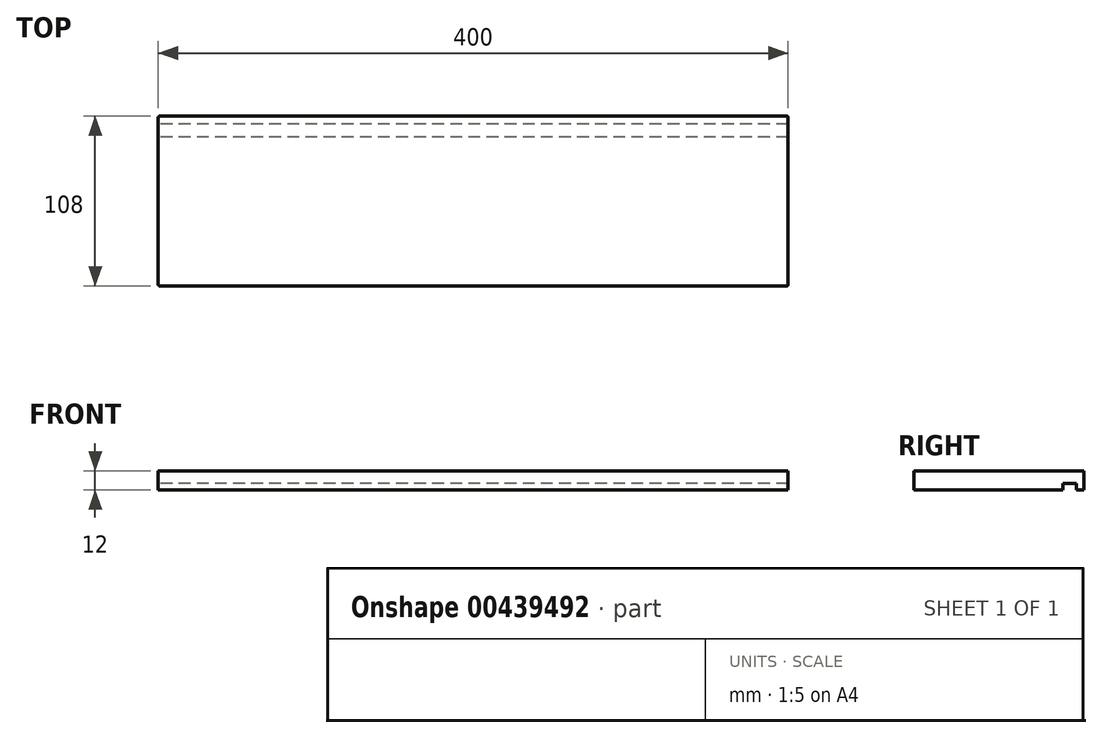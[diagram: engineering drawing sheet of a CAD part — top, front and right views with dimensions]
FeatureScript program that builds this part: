
annotation { "Feature Type Name" : "Feature", "Feature Type Description" : "" }
export const myFeature = defineFeature(function(context is Context, id is Id, definition is map)
    precondition{}
    {
        {
            var Q0;
            Q0=qCreatedBy(makeId("Right.planeOp"),FACE);
            var sketch = newSketch(context, id + "F0", { "sketchPlane" : qUnion([Q0])});
            skLineSegment(sketch, "E0.top", {"start": v(0, 12) * mm, "end": v(108, 12) * mm});
            skLineSegment(sketch, "E0.left", {"start": v(0, 0) * mm, "end": v(0, 12) * mm});
            skLineSegment(sketch, "E0.right", {"start": v(108, 0) * mm, "end": v(108, 12) * mm});
            skLineSegment(sketch, "E1", {"start": v(108, 0) * mm, "end": v(103, 0) * mm});
            skLineSegment(sketch, "E2", {"start": v(103, 0) * mm, "end": v(103, 4) * mm});
            skLineSegment(sketch, "E3", {"start": v(103, 4) * mm, "end": v(94.5, 4) * mm});
            skLineSegment(sketch, "E4", {"start": v(94.5, 4) * mm, "end": v(94.5, 0) * mm});
            skLineSegment(sketch, "E5", {"start": v(94.5, 0) * mm, "end": v(0, 0) * mm});
            skSolve(sketch);
        }
        {
            var Q0;
            Q0=makeQuery(id+"F0.imprint","IMPRINT",FACE,{"disambiguationData":[TD([[makeQuery(id+"F0.imprint","IMPRINT",EDGE,{"derivedFrom":sQuery(id+"F0.wireOp",EDGE,"E0.top")}),-1.0]])]});
            extrude(context, id + "F1", {"entities" : qUnion([Q0]), "depth" : 400 * mm, "offsetDistance" : 25 * mm, "symmetric" : true});
        }
        {
            var Q0;
            Q0=makeQuery(id+"F1.opExtrude","CAP_EDGE",EDGE,{"disambiguationData":[OSD([sQuery(id+"F0.wireOp",EDGE,"E0.left")])],"isStart":false});
            var Q1;
            Q1=makeQuery(id+"F1.opExtrude","CAP_EDGE",EDGE,{"disambiguationData":[OSD([sQuery(id+"F0.wireOp",EDGE,"E0.right")])],"isStart":false});
            var Q2;
            Q2=makeQuery(id+"F1.opExtrude","CAP_EDGE",EDGE,{"disambiguationData":[OSD([sQuery(id+"F0.wireOp",EDGE,"E0.right")])],"isStart":true});
            var Q3;
            Q3=makeQuery(id+"F1.opExtrude","CAP_EDGE",EDGE,{"disambiguationData":[OSD([sQuery(id+"F0.wireOp",EDGE,"E0.left")])],"isStart":true});
            fillet(context, id + "F2", {"entities" : qUnion([Q0, Q1, Q2, Q3]), "radius" : 1 * mm, "tangentPropagation" : true, "allowEdgeOverflow" : false});
        }
    });
